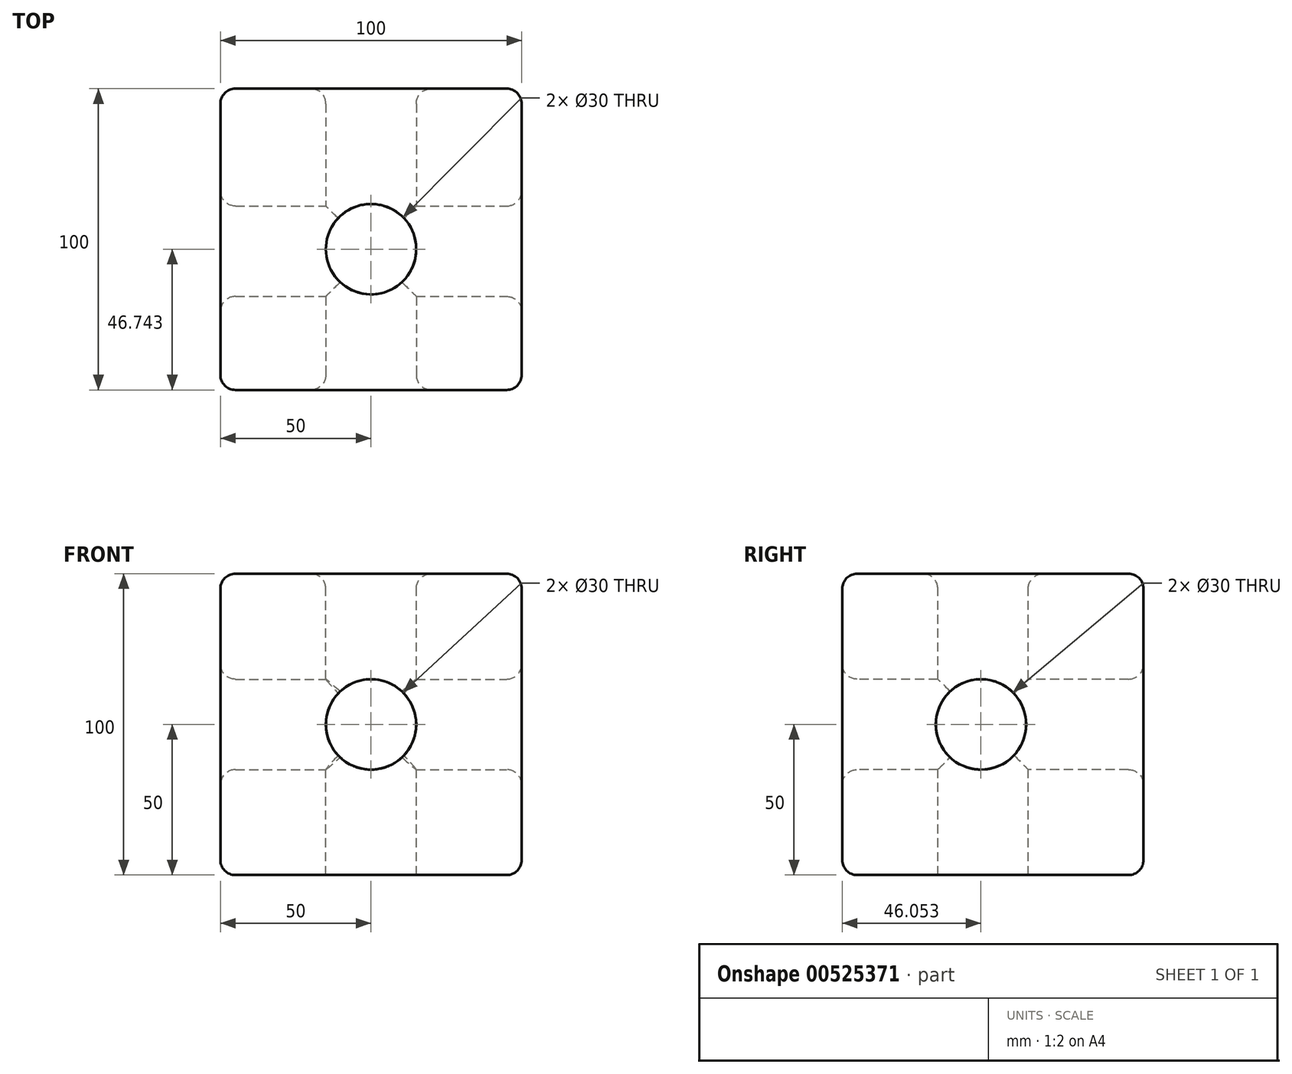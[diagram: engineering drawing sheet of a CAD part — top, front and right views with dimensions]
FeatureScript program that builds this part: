
annotation { "Feature Type Name" : "Feature", "Feature Type Description" : "" }
export const myFeature = defineFeature(function(context is Context, id is Id, definition is map)
    precondition{}
    {
        {
            var Q0;
            Q0=qCreatedBy(makeId("Front.planeOp"),FACE);
            var sketch = newSketch(context, id + "F0", { "sketchPlane" : qUnion([Q0])});
            skLineSegment(sketch, "E0.bottom", {"start": v(50, 50) * mm, "end": v(-50, 50) * mm});
            skLineSegment(sketch, "E0.top", {"start": v(50, -50) * mm, "end": v(-50, -50) * mm});
            skLineSegment(sketch, "E0.left", {"start": v(50, 50) * mm, "end": v(50, -50) * mm});
            skLineSegment(sketch, "E0.right", {"start": v(-50, 50) * mm, "end": v(-50, -50) * mm});
            skPoint(sketch, "E0.middle", {"position": v(0, 0) * mm});
            skSolve(sketch);
        }
        {
            var Q0;
            Q0=makeQuery(id+"F0.imprint","IMPRINT",FACE,{"disambiguationData":[TD([[makeQuery(id+"F0.imprint","IMPRINT",EDGE,{"derivedFrom":sQuery(id+"F0.wireOp",EDGE,"E0.bottom")}),1.0]])]});
            extrude(context, id + "F1", {"entities" : qUnion([Q0]), "depth" : 100 * mm, "offsetDistance" : 25 * mm});
        }
        {
            var Q0;
            Q0=makeQuery(id+"F1.opExtrude","CAP_FACE",FACE,{"disambiguationData":[OSD([sQuery(id+"F0.wireOp",EDGE,"E0.bottom"),sQuery(id+"F0.wireOp",EDGE,"E0.top"),sQuery(id+"F0.wireOp",EDGE,"E0.left"),sQuery(id+"F0.wireOp",EDGE,"E0.right")])],"isStart":false});
            var sketch = newSketch(context, id + "F2", { "sketchPlane" : qUnion([Q0])});
            skCircle(sketch, "E1", {"center": v(0, 0) * mm, "radius": 15 * mm});
            skSolve(sketch);
        }
        {
            var Q0;
            Q0=makeQuery(id+"F2.imprint","IMPRINT",FACE,{"disambiguationData":[TD([[makeQuery(id+"F2.imprint","IMPRINT",EDGE,{"derivedFrom":sQuery(id+"F2.wireOp",EDGE,"E1")}),1.0]])]});
            extrude(context, id + "F3", {"entities" : qUnion([Q0]), "operationType" : NewBodyOperationType.REMOVE, "oppositeDirection" : true, "depth" : 100 * mm, "offsetDistance" : 25 * mm});
        }
        {
            var Q0;
            Q0=makeQuery(id+"F1.opExtrude","SWEPT_FACE",FACE,{"disambiguationData":[OSD([sQuery(id+"F0.wireOp",EDGE,"E0.bottom")])]});
            var sketch = newSketch(context, id + "F4", { "sketchPlane" : qUnion([Q0])});
            skCircle(sketch, "E2", {"center": v(0, -53.26) * mm, "radius": 15 * mm});
            skSolve(sketch);
        }
        {
            var Q0;
            Q0=makeQuery(id+"F4.imprint","IMPRINT",FACE,{"disambiguationData":[TD([[makeQuery(id+"F4.imprint","IMPRINT",EDGE,{"derivedFrom":sQuery(id+"F4.wireOp",EDGE,"E2")}),1.0]])]});
            extrude(context, id + "F5", {"entities" : qUnion([Q0]), "operationType" : NewBodyOperationType.REMOVE, "oppositeDirection" : true, "depth" : 100 * mm, "offsetDistance" : 25 * mm});
        }
        {
            var Q0;
            Q0=makeQuery(id+"F1.opExtrude","SWEPT_FACE",FACE,{"disambiguationData":[OSD([sQuery(id+"F0.wireOp",EDGE,"E0.left")])]});
            var sketch = newSketch(context, id + "F6", { "sketchPlane" : qUnion([Q0])});
            skCircle(sketch, "E3", {"center": v(-53.95, 0) * mm, "radius": 15 * mm});
            skSolve(sketch);
        }
        {
            var Q0;
            Q0=makeQuery(id+"F6.imprint","IMPRINT",FACE,{"disambiguationData":[TD([[makeQuery(id+"F6.imprint","IMPRINT",EDGE,{"derivedFrom":sQuery(id+"F6.wireOp",EDGE,"E3")}),1.0]])]});
            extrude(context, id + "F7", {"entities" : qUnion([Q0]), "operationType" : NewBodyOperationType.REMOVE, "oppositeDirection" : true, "depth" : 100 * mm, "offsetDistance" : 25 * mm});
        }
        {
            var Q0;
            Q0=makeQuery(id+"F1.opExtrude","CAP_FACE",FACE,{"disambiguationData":[OSD([sQuery(id+"F0.wireOp",EDGE,"E0.bottom"),sQuery(id+"F0.wireOp",EDGE,"E0.top"),sQuery(id+"F0.wireOp",EDGE,"E0.left"),sQuery(id+"F0.wireOp",EDGE,"E0.right")])],"isStart":false});
            var Q1;
            Q1=makeQuery(id+"F1.opExtrude","SWEPT_FACE",FACE,{"disambiguationData":[OSD([sQuery(id+"F0.wireOp",EDGE,"E0.right")])]});
            var Q2;
            Q2=makeQuery(id+"F1.opExtrude","SWEPT_FACE",FACE,{"disambiguationData":[OSD([sQuery(id+"F0.wireOp",EDGE,"E0.left")])]});
            var Q3;
            Q3=makeQuery(id+"F3.boolean.opBoolean","COPY",EDGE,{"derivedFrom":makeQuery(id+"F3.opExtrude","CAP_EDGE",EDGE,{"disambiguationData":[OSD([sQuery(id+"F2.wireOp",EDGE,"E1")])],"isStart":false})});
            var Q4;
            Q4=makeQuery(id+"F1.opExtrude","CAP_FACE",FACE,{"disambiguationData":[OSD([sQuery(id+"F0.wireOp",EDGE,"E0.bottom"),sQuery(id+"F0.wireOp",EDGE,"E0.top"),sQuery(id+"F0.wireOp",EDGE,"E0.left"),sQuery(id+"F0.wireOp",EDGE,"E0.right")])],"isStart":true});
            fillet(context, id + "F8", {"entities" : qUnion([Q0, Q1, Q2, Q3, Q4]), "radius" : 5 * mm, "tangentPropagation" : true, "allowEdgeOverflow" : false});
        }
        {
            var Q0;
            Q0=makeQuery(id+"F5.boolean.opBoolean","COPY",EDGE,{"derivedFrom":makeQuery(id+"F5.opExtrude","CAP_EDGE",EDGE,{"disambiguationData":[OSD([sQuery(id+"F4.wireOp",EDGE,"E2")])],"isStart":true})});
            var Q1;
            Q1=makeQuery(id+"F1.opExtrude","SWEPT_FACE",FACE,{"disambiguationData":[OSD([sQuery(id+"F0.wireOp",EDGE,"E0.bottom")])]});
            var Q2;
            Q2=makeQuery(id+"F5.boolean.opBoolean","COPY",EDGE,{"derivedFrom":makeQuery(id+"F5.opExtrude","CAP_EDGE",EDGE,{"disambiguationData":[OSD([sQuery(id+"F4.wireOp",EDGE,"E2")])],"isStart":false})});
            fillet(context, id + "F9", {"entities" : qUnion([Q0, Q1, Q2]), "radius" : 5 * mm, "tangentPropagation" : true, "allowEdgeOverflow" : false});
        }
    });
